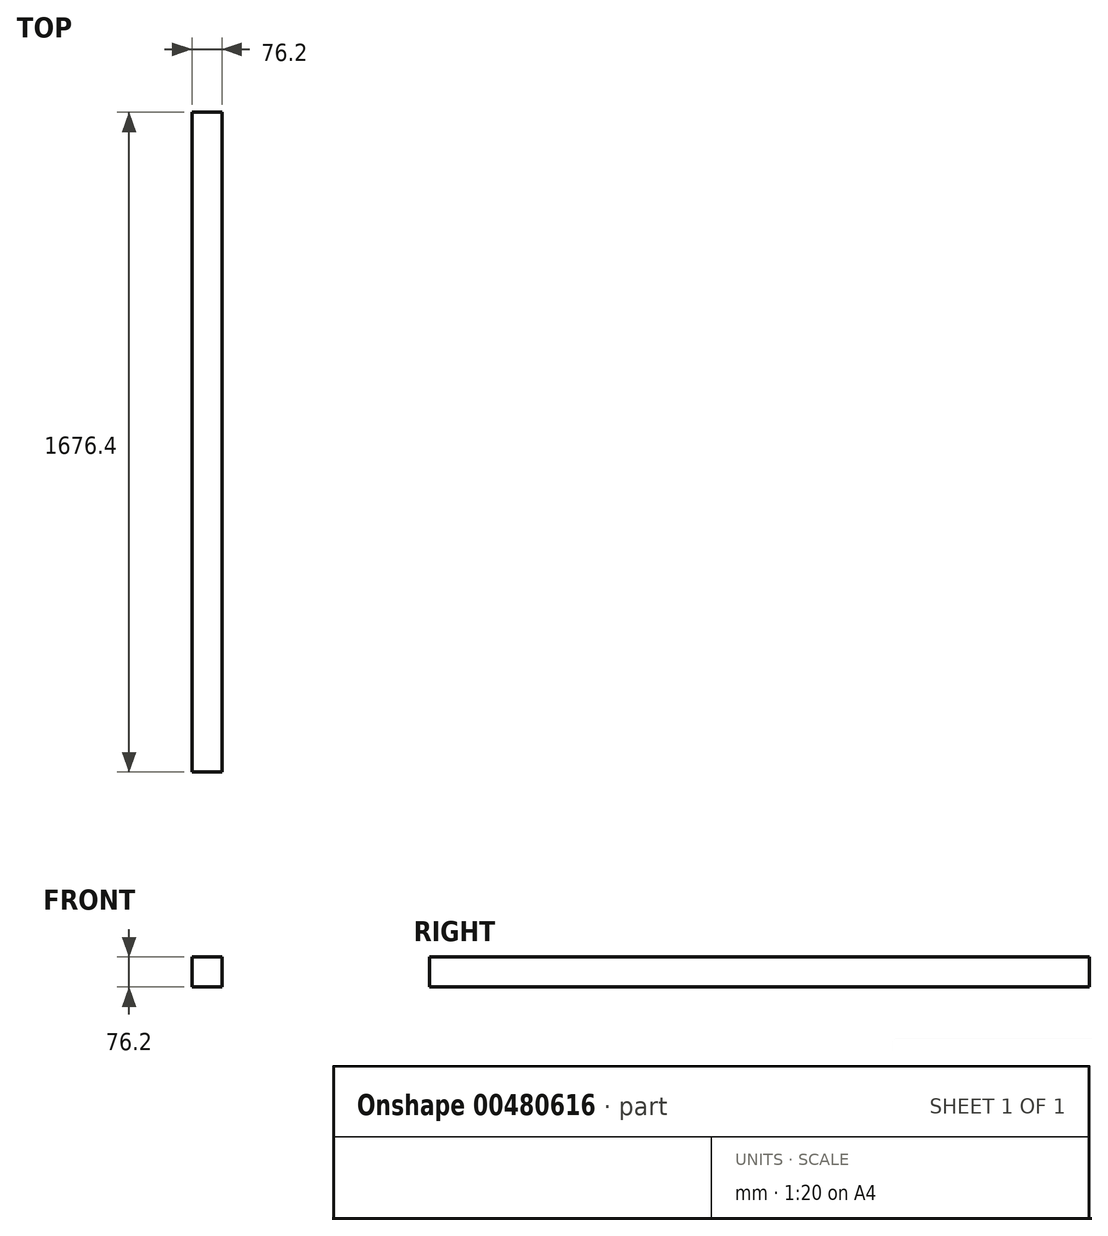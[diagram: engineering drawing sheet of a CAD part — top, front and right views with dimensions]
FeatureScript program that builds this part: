
annotation { "Feature Type Name" : "Feature", "Feature Type Description" : "" }
export const myFeature = defineFeature(function(context is Context, id is Id, definition is map)
    precondition{}
    {
        {
            var Q0;
            Q0=qCreatedBy(makeId("Front.planeOp"),FACE);
            var sketch = newSketch(context, id + "F0", { "sketchPlane" : qUnion([Q0])});
            skLineSegment(sketch, "E0.bottom", {"start": v(38.1, 38.1) * mm, "end": v(-38.1, 38.1) * mm});
            skLineSegment(sketch, "E0.top", {"start": v(38.1, -38.1) * mm, "end": v(-38.1, -38.1) * mm});
            skLineSegment(sketch, "E0.left", {"start": v(38.1, 38.1) * mm, "end": v(38.1, -38.1) * mm});
            skLineSegment(sketch, "E0.right", {"start": v(-38.1, 38.1) * mm, "end": v(-38.1, -38.1) * mm});
            skPoint(sketch, "E0.middle", {"position": v(0, 0) * mm});
            skSolve(sketch);
        }
        {
            var Q0;
            Q0 = qSketchRegion(id + "F0", true);
            extrude(context, id + "F1", {"entities" : qUnion([Q0]), "depth" : 1676.4 * mm});
        }
    });
